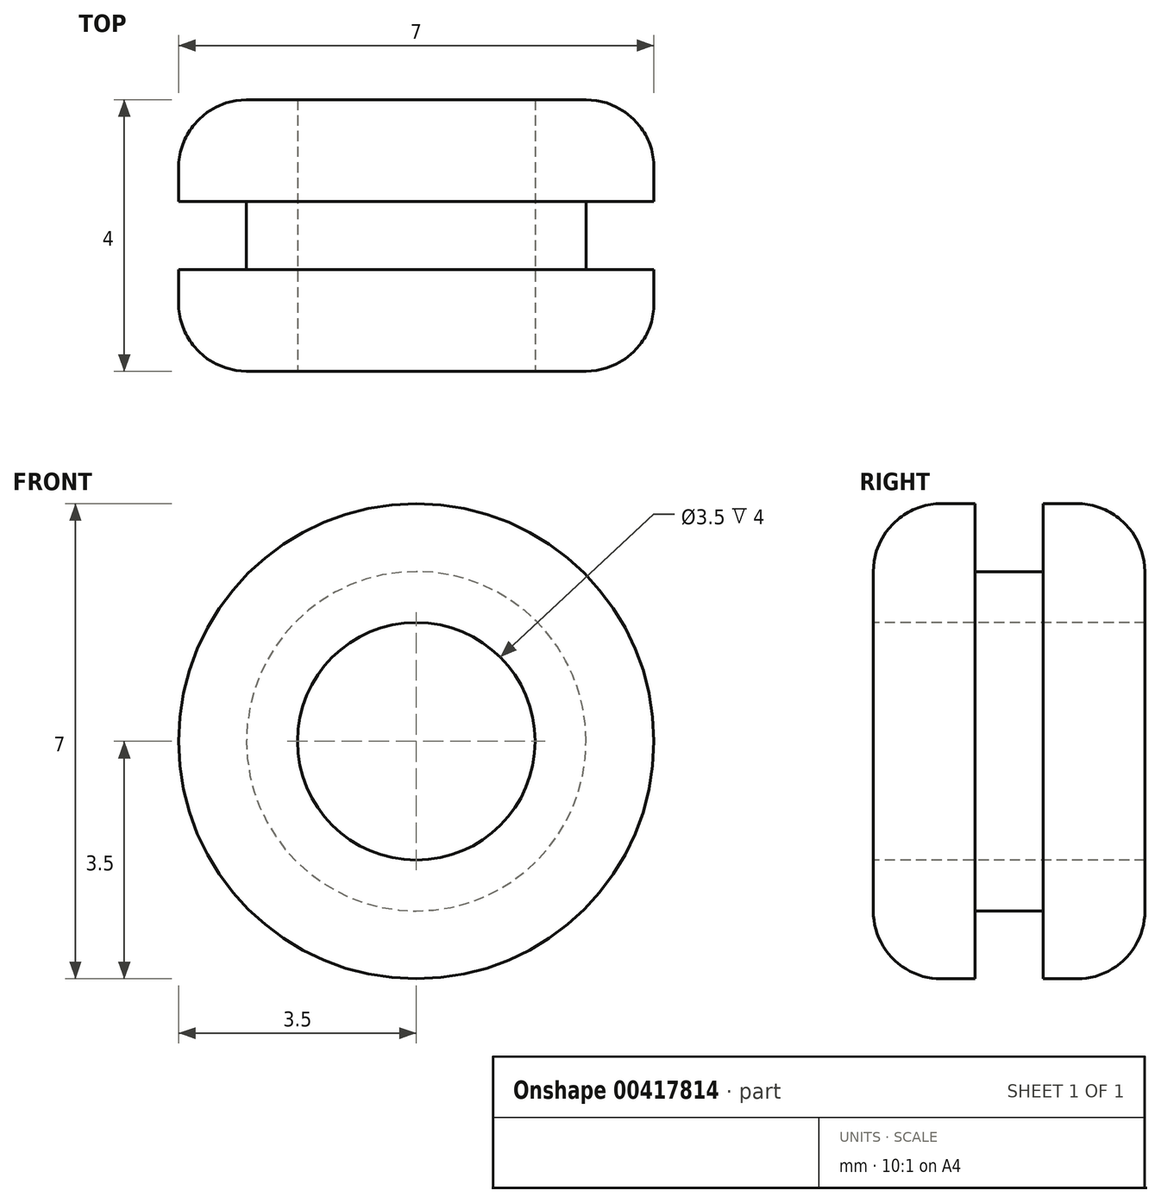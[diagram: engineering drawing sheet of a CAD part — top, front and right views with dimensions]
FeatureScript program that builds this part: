
annotation { "Feature Type Name" : "Feature", "Feature Type Description" : "" }
export const myFeature = defineFeature(function(context is Context, id is Id, definition is map)
    precondition{}
    {
        {
            var Q0;
            Q0=qCreatedBy(makeId("Front.planeOp"),FACE);
            var sketch = newSketch(context, id + "F0", { "sketchPlane" : qUnion([Q0])});
            skCircle(sketch, "E0", {"center": v(0, 0) * mm, "radius": 3.5 * mm});
            skSolve(sketch);
        }
        {
            var Q0;
            Q0=makeQuery(id+"F0.imprint","IMPRINT",FACE,{"disambiguationData":[TD([[makeQuery(id+"F0.imprint","IMPRINT",EDGE,{"derivedFrom":sQuery(id+"F0.wireOp",EDGE,"E0")}),1.0]])]});
            extrude(context, id + "F1", {"entities" : qUnion([Q0]), "depth" : 1.5 * mm});
        }
        {
            var Q0;
            Q0=makeQuery(id+"F1.opExtrude","CAP_FACE",FACE,{"disambiguationData":[OSD([sQuery(id+"F0.wireOp",EDGE,"E0")])],"isStart":false});
            var sketch = newSketch(context, id + "F2", { "sketchPlane" : qUnion([Q0])});
            skCircle(sketch, "E1", {"center": v(0, 0) * mm, "radius": 2.5 * mm});
            skSolve(sketch);
        }
        {
            var Q0;
            Q0=makeQuery(id+"F2.imprint","IMPRINT",FACE,{"disambiguationData":[TD([[makeQuery(id+"F2.imprint","IMPRINT",EDGE,{"derivedFrom":sQuery(id+"F2.wireOp",EDGE,"E1")}),1.0]])]});
            extrude(context, id + "F3", {"entities" : qUnion([Q0]), "operationType" : NewBodyOperationType.ADD, "depth" : 1 * mm});
        }
        {
            var Q0;
            Q0=makeQuery(id+"F3.opExtrude","CAP_FACE",FACE,{"disambiguationData":[OSD([sQuery(id+"F2.wireOp",EDGE,"E1")])],"isStart":false});
            var sketch = newSketch(context, id + "F4", { "sketchPlane" : qUnion([Q0])});
            skCircle(sketch, "E2", {"center": v(0, 0) * mm, "radius": 3.5 * mm});
            skSolve(sketch);
        }
        {
            var Q0;
            Q0=makeQuery(id+"F4.imprint","IMPRINT",FACE,{"disambiguationData":[TD([[makeQuery(id+"F4.imprint","IMPRINT",EDGE,{"derivedFrom":sQuery(id+"F4.wireOp",EDGE,"E2")}),1.0]])]});
            var Q1;
            Q1=makeQuery(id+"F4.imprint","IMPRINT",FACE,{"disambiguationData":[TD([[makeQuery(id+"F4.imprint","IMPRINT",EDGE,{"derivedFrom":makeQuery(id+"F3.opExtrude","CAP_EDGE",EDGE,{"disambiguationData":[OSD([sQuery(id+"F2.wireOp",EDGE,"E1")])],"isStart":false})}),1.0]])]});
            var Q2;
            Q2=sQuery(id+"F4.wireOp",EDGE,"E2");
            extrude(context, id + "F5", {"entities" : qUnion([Q0, Q1]), "surfaceEntities" : qUnion([Q2]), "depth" : 1.5 * mm});
        }
        {
            var Q0;
            Q0=makeQuery(id+"F5.opExtrude","CAP_EDGE",EDGE,{"disambiguationData":[OSD([sQuery(id+"F4.wireOp",EDGE,"E2")])],"isStart":false});
            fillet(context, id + "F6", {"entities" : qUnion([Q0]), "radius" : 1 * mm, "tangentPropagation" : true, "allowEdgeOverflow" : false});
        }
        {
            var Q0;
            Q0=makeQuery(id+"F1.opExtrude","CAP_EDGE",EDGE,{"disambiguationData":[OSD([sQuery(id+"F0.wireOp",EDGE,"E0")])],"isStart":true});
            fillet(context, id + "F7", {"entities" : qUnion([Q0]), "radius" : 1 * mm, "tangentPropagation" : true, "allowEdgeOverflow" : false});
        }
        {
            var Q0;
            Q0=makeQuery(id+"F5.opExtrude","CAP_FACE",FACE,{"disambiguationData":[OSD([sQuery(id+"F4.wireOp",EDGE,"E2")])],"isStart":false});
            var sketch = newSketch(context, id + "F8", { "sketchPlane" : qUnion([Q0])});
            skCircle(sketch, "E3", {"center": v(0, 0) * mm, "radius": 1.75 * mm});
            skSolve(sketch);
        }
        {
            var Q0;
            Q0=makeQuery(id+"F5.opExtrude","SWEPT_BODY",BODY,{"disambiguationData":[OSD([sQuery(id+"F4.wireOp",EDGE,"E2")])]});
            deleteBodies(context, id + "F9", {"entities" : qUnion([Q0])});
        }
        {
            var Q0;
            Q0=makeQuery(id+"F3.opExtrude","CAP_FACE",FACE,{"disambiguationData":[OSD([sQuery(id+"F2.wireOp",EDGE,"E1")])],"isStart":false});
            var sketch = newSketch(context, id + "F10", { "sketchPlane" : qUnion([Q0])});
            skCircle(sketch, "E4", {"center": v(0, 0) * mm, "radius": 3.5 * mm});
            skSolve(sketch);
        }
        {
            var Q0;
            Q0 = qSketchRegion(id + "F10", true);
            extrude(context, id + "F11", {"entities" : qUnion([Q0]), "operationType" : NewBodyOperationType.ADD, "depth" : 1.5 * mm});
        }
        {
            var Q0;
            Q0=makeQuery(id+"F11.opExtrude","CAP_EDGE",EDGE,{"disambiguationData":[OSD([sQuery(id+"F10.wireOp",EDGE,"E4")])],"isStart":false});
            fillet(context, id + "F12", {"entities" : qUnion([Q0]), "radius" : 1 * mm, "tangentPropagation" : true, "allowEdgeOverflow" : false});
        }
        {
            var Q0;
            Q0=sQuery(id+"F8.wireOp",VERTEX,"E3.center");
            var Q1;
            Q1=makeQuery(id+"F1.opExtrude","SWEPT_BODY",BODY,{"disambiguationData":[OSD([sQuery(id+"F0.wireOp",EDGE,"E0")])]});
            hole(context, id + "F13", {"style" : HoleStyle.SIMPLE, "endStyle" : HoleEndStyle.THROUGH, "holeDiameter" : 3.5 * mm, "isTappedThrough" : true, "tappedDepth" : 12 * mm, "tapClearance" : 3, "locations" : qUnion([Q0]), "scope" : qUnion([Q1])});
        }
    });
